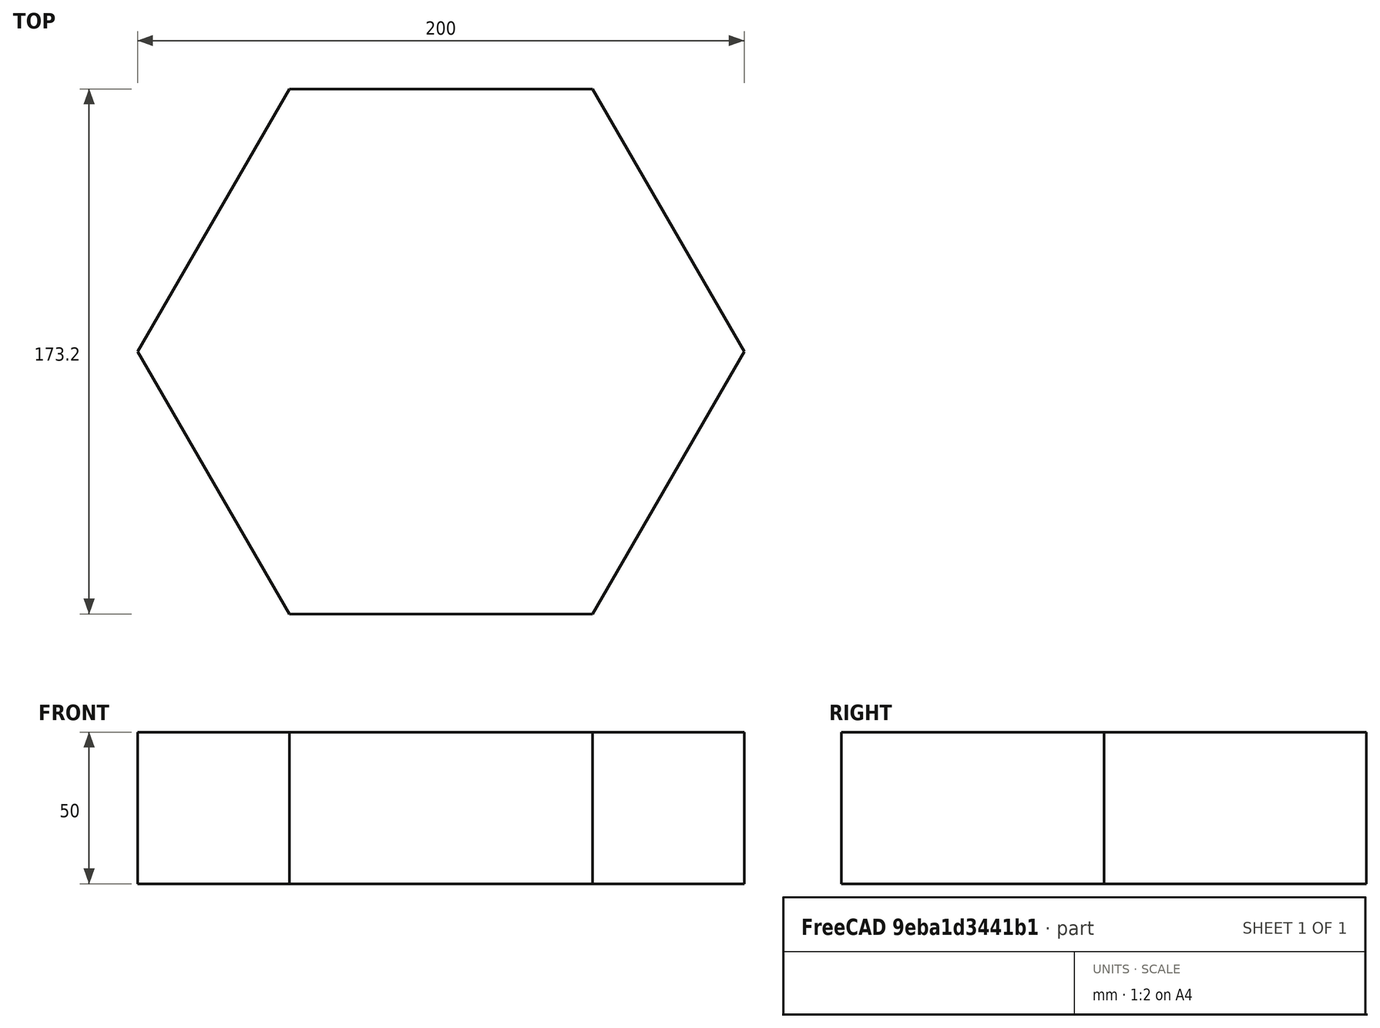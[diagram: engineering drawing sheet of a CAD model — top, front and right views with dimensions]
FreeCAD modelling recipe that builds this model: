
FCSTD DOCUMENT  (FreeCAD 1.0R38806 (Git))
Label: Opgave_2.0.2
License: All rights reserved
LicenseURL: http://en.wikipedia.org/wiki/All_rights_reserved
objects: Sketcher::SketchObject×2, PartDesign::Pad×1, PartDesign::Body×1
note: 8 computed .brp shape members not serialized (recipe doc carries the construction recipe); baked Part::Feature solids carry a one-line shape summary decoded from their .brp

FEATURE [Sketcher::SketchObject] Sketch
  ArcFitTolerance = 1e-06
  AttachmentSupport = -> [XY_Plane]
  FullyConstrained = true
  MakeInternals = false
  MapMode = 5
  sketch-geometry (7):
    g0: LineSegment StartX=100 StartY=0 StartZ=0 EndX=50 EndY=86.6025 EndZ=0
    g1: LineSegment StartX=50 StartY=86.6025 StartZ=0 EndX=-50 EndY=86.6025 EndZ=0
    g2: LineSegment StartX=-50 StartY=86.6025 StartZ=0 EndX=-100 EndY=1.42e-14 EndZ=0
    g3: LineSegment StartX=-100 StartY=1.42e-14 StartZ=0 EndX=-50 EndY=-86.6025 EndZ=0
    g4: LineSegment StartX=-50 StartY=-86.6025 StartZ=0 EndX=50 EndY=-86.6025 EndZ=0
    g5: LineSegment StartX=50 StartY=-86.6025 StartZ=0 EndX=100 EndY=0 EndZ=0
    g6: Circle [constr] CenterX=0 CenterY=0 CenterZ=0 NormalX=0 NormalY=0 NormalZ=1 AngleXU=0 Radius=100
  constraints (16):
    c: Coincident(g0,g1)
    c: Coincident(g1,g2)
    c: Coincident(g2,g3)
    c: Coincident(g3,g4)
    c: Coincident(g4,g5)
    c: Coincident(g5,g0)
    c: Equal(g0, g1-g5) x5
    c: PointOnObject(g0,g6)
    c: PointOnObject(g1,g6)
    c: PointOnObject(g2,g6)
    c: PointOnObject(g3,g6)
    c: PointOnObject(g4,g6)
    c: PointOnObject(g5,g6)
    c: Coincident(g6,g-1)
    c: PointOnObject(g5,g-1)
    c: Diameter(g6) = 200
FEATURE [PartDesign::Pad] Pad
  Direction = (0,0,1)
  Length = 50
  Length2 = 10
  Profile = -> Sketch
  ReferenceAxis = -> Sketch [N_Axis]
  Refine = true
  Suppressed = false
  Type = 0
FEATURE [Sketcher::SketchObject] Sketch001
  ArcFitTolerance = 1e-06
  AttachmentSupport = -> [Pad]
  FullyConstrained = false
  MakeInternals = false
  MapMode = 5
  Placement = pos=(0,-86.6025,0) rot=(1,0,0;1.5708rad)
  sketch-geometry (5):
    g0: Circle CenterX=-25 CenterY=25 CenterZ=0 NormalX=0 NormalY=0 NormalZ=1 AngleXU=0 Radius=12.5
    g1: ArcOfCircle CenterX=15.198 CenterY=33.2499 CenterZ=0 NormalX=0 NormalY=0 NormalZ=1 AngleXU=0 Radius=10 StartAngle=0.896756 EndAngle=4.03835
    g2: ArcOfCircle CenterX=30.8242 CenterY=20.7669 CenterZ=0 NormalX=0 NormalY=0 NormalZ=1 AngleXU=0 Radius=10 StartAngle=4.03835 EndAngle=7.17994
    g3: LineSegment StartX=21.4395 StartY=41.063 StartZ=0 EndX=37.0656 EndY=28.58 EndZ=0
    g4: LineSegment StartX=8.95655 StartY=25.4368 StartZ=0 EndX=24.5827 EndY=12.9539 EndZ=0
  constraints (10):
    c: Tangent(g1,g3) = 1.5708
    c: Tangent(g1,g4) = -1.5708
    c: Tangent(g2,g3) = 1.5708
    c: Tangent(g2,g4) = -1.5708
    c: Equal(g1,g2)
    c: DistanceY(g-1,g0) = 25
    c: DistanceX(g0,g-1) = 25
    c: Diameter(g0) = 25
    c: Radius(g2) = 10
    c: Distance(g1,g2) = 20
FEATURE [PartDesign::Body] Body
  AllowCompound = true
  Group = -> [Sketch,Pad,Sketch001]
  Origin = -> Origin
  Tip = -> Pad
